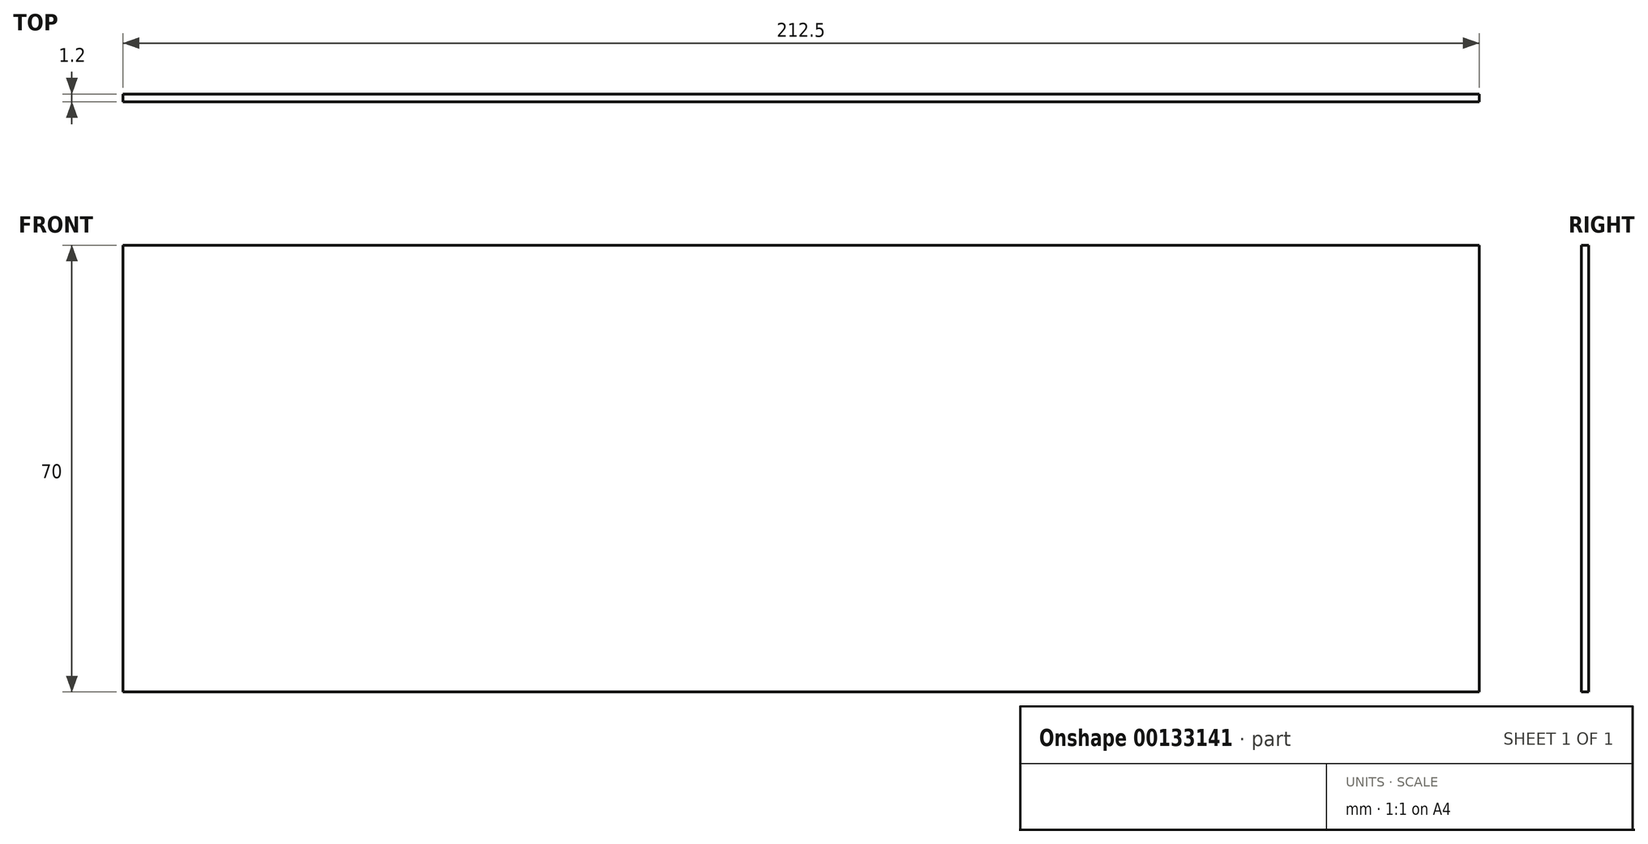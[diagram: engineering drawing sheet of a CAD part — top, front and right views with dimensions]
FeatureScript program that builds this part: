
annotation { "Feature Type Name" : "Feature", "Feature Type Description" : "" }
export const myFeature = defineFeature(function(context is Context, id is Id, definition is map)
    precondition{}
    {
        {
            var Q0;
            Q0=qCreatedBy(makeId("Front.planeOp"),FACE);
            var sketch = newSketch(context, id + "F0", { "sketchPlane" : qUnion([Q0])});
            skLineSegment(sketch, "E0.bottom", {"start": v(-106.25, 35) * mm, "end": v(106.25, 35) * mm});
            skLineSegment(sketch, "E0.top", {"start": v(-106.25, -35) * mm, "end": v(106.25, -35) * mm});
            skLineSegment(sketch, "E0.left", {"start": v(-106.25, 35) * mm, "end": v(-106.25, -35) * mm});
            skLineSegment(sketch, "E0.right", {"start": v(106.25, 35) * mm, "end": v(106.25, -35) * mm});
            skPoint(sketch, "E0.middle", {"position": v(0, 0) * mm});
            skSolve(sketch);
        }
        {
            var Q0;
            Q0=makeQuery(id+"F0.imprint","IMPRINT",FACE,{"disambiguationData":[TD([[makeQuery(id+"F0.imprint","IMPRINT",EDGE,{"derivedFrom":sQuery(id+"F0.wireOp",EDGE,"E0.bottom")}),-1.0]])]});
            extrude(context, id + "F1", {"entities" : qUnion([Q0]), "depth" : 1.2 * mm});
        }
    });
